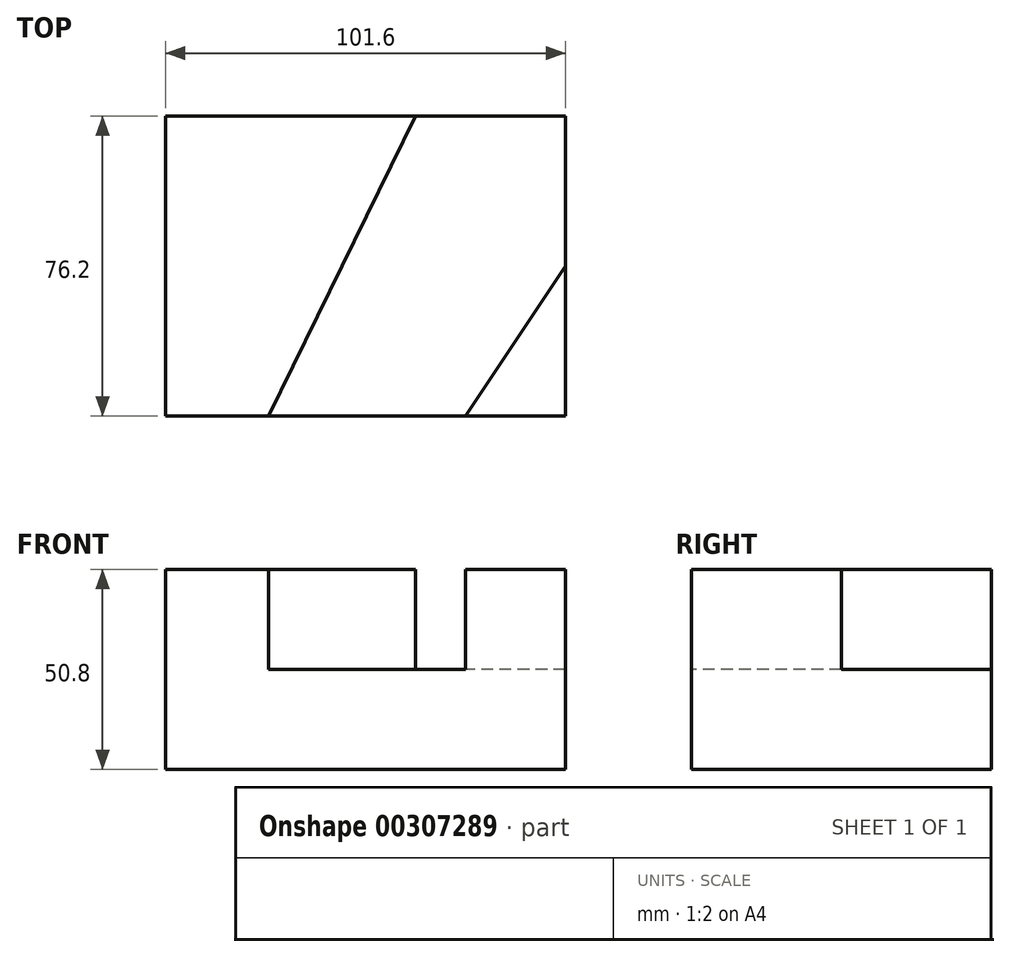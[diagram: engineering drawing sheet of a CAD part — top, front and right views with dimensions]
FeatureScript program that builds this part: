
annotation { "Feature Type Name" : "Feature", "Feature Type Description" : "" }
export const myFeature = defineFeature(function(context is Context, id is Id, definition is map)
    precondition{}
    {
        {
            var Q0;
            Q0=qCreatedBy(makeId("Front.planeOp"),FACE);
            var sketch = newSketch(context, id + "F0", { "sketchPlane" : qUnion([Q0])});
            skLineSegment(sketch, "E0", {"start": v(-41.12, 8.11) * mm, "end": v(-41.12, -17.29) * mm});
            skLineSegment(sketch, "E1", {"start": v(-41.12, -17.29) * mm, "end": v(60.48, -17.29) * mm});
            skLineSegment(sketch, "E2", {"start": v(60.48, -17.29) * mm, "end": v(60.48, 8.11) * mm});
            skLineSegment(sketch, "E3", {"start": v(60.48, 8.11) * mm, "end": v(-41.12, 8.11) * mm});
            skSolve(sketch);
        }
        {
            var Q0;
            Q0=makeQuery(id+"F0.imprint","IMPRINT",FACE,{"disambiguationData":[TD([[makeQuery(id+"F0.imprint","IMPRINT",EDGE,{"derivedFrom":sQuery(id+"F0.wireOp",EDGE,"E0")}),1.0]])]});
            extrude(context, id + "F1", {"entities" : qUnion([Q0]), "depth" : 76.2 * mm});
        }
        {
            var Q0;
            Q0=makeQuery(id+"F1.opExtrude","SWEPT_FACE",FACE,{"disambiguationData":[OSD([sQuery(id+"F0.wireOp",EDGE,"E3")])]});
            var sketch = newSketch(context, id + "F2", { "sketchPlane" : qUnion([Q0])});
            skLineSegment(sketch, "E4", {"start": v(35.08, -76.2) * mm, "end": v(60.48, -76.2) * mm});
            skLineSegment(sketch, "E5", {"start": v(60.48, -76.2) * mm, "end": v(60.48, -38.1) * mm});
            skLineSegment(sketch, "E6", {"start": v(60.48, -38.1) * mm, "end": v(35.08, -76.2) * mm});
            skSolve(sketch);
        }
        {
            var Q0;
            Q0 = qSketchRegion(id + "F2", true);
            extrude(context, id + "F3", {"entities" : qUnion([Q0]), "operationType" : NewBodyOperationType.ADD, "depth" : 25.4 * mm});
        }
        {
            var Q0;
            Q0=makeQuery(id+"F1.opExtrude","SWEPT_FACE",FACE,{"disambiguationData":[OSD([sQuery(id+"F0.wireOp",EDGE,"E3")])]});
            var sketch = newSketch(context, id + "F4", { "sketchPlane" : qUnion([Q0])});
            skLineSegment(sketch, "E7", {"start": v(-41.12, -76.2) * mm, "end": v(-14.95, -76.2) * mm});
            skLineSegment(sketch, "E8", {"start": v(-41.12, -76.2) * mm, "end": v(-41.12, 0) * mm});
            skLineSegment(sketch, "E9", {"start": v(-41.12, 0) * mm, "end": v(22.38, 0) * mm});
            skLineSegment(sketch, "E10", {"start": v(22.38, 0) * mm, "end": v(-14.95, -76.2) * mm});
            skSolve(sketch);
        }
        {
            var Q0;
            Q0=makeQuery(id+"F4.imprint","IMPRINT",FACE,{"disambiguationData":[TD([[makeQuery(id+"F4.imprint","IMPRINT",EDGE,{"derivedFrom":sQuery(id+"F4.wireOp",EDGE,"E7")}),-1.0]])]});
            extrude(context, id + "F5", {"entities" : qUnion([Q0]), "operationType" : NewBodyOperationType.ADD, "depth" : 25.4 * mm});
        }
    });
